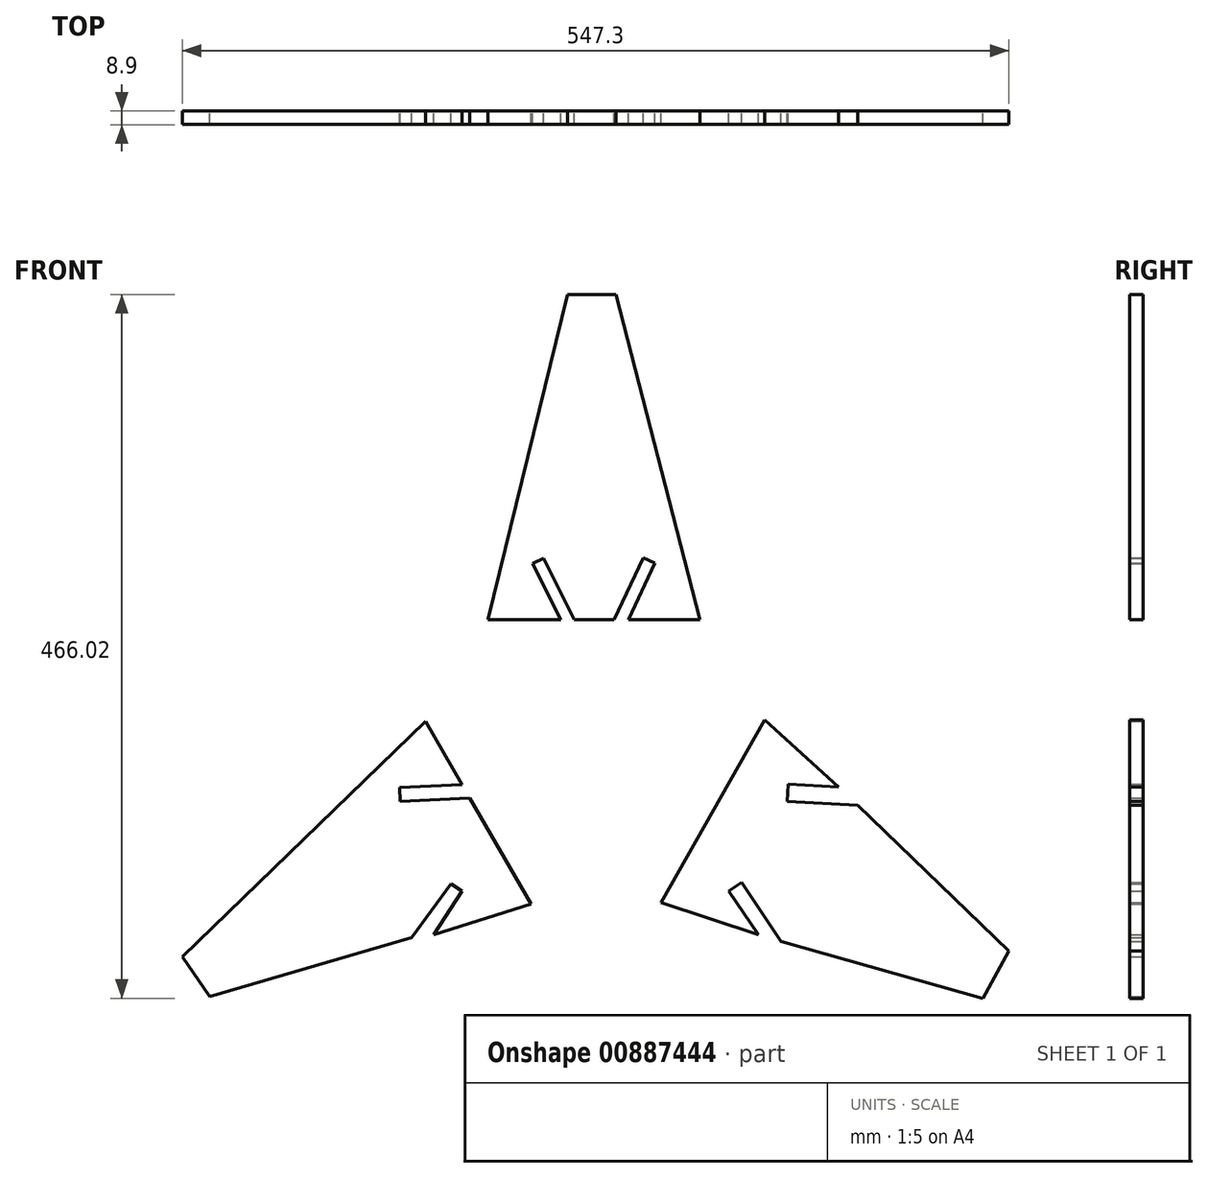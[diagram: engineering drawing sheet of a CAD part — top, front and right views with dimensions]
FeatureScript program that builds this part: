
annotation { "Feature Type Name" : "Feature", "Feature Type Description" : "" }
export const myFeature = defineFeature(function(context is Context, id is Id, definition is map)
    precondition{}
    {
        {
            var Q0;
            Q0=qCreatedBy(makeId("Front.planeOp"),FACE);
            var sketch = newSketch(context, id + "F0", { "sketchPlane" : qUnion([Q0])});
            skLineSegment(sketch, "E0", {"start": v(198.95, 271.23) * mm, "end": v(223.16, 229.27) * mm});
            skLineSegment(sketch, "E1", {"start": v(268.64, 150.43) * mm, "end": v(204.33, 130.14) * mm});
            skLineSegment(sketch, "E2", {"start": v(204.33, 130.14) * mm, "end": v(223.16, 158.75) * mm});
            skLineSegment(sketch, "E3", {"start": v(223.16, 158.75) * mm, "end": v(215.63, 163.7) * mm});
            skLineSegment(sketch, "E4", {"start": v(215.63, 163.7) * mm, "end": v(189.66, 127.94) * mm});
            skLineSegment(sketch, "E5", {"start": v(189.66, 127.94) * mm, "end": v(55.9, 89.06) * mm});
            skLineSegment(sketch, "E6", {"start": v(55.9, 89.06) * mm, "end": v(37.81, 115.47) * mm});
            skLineSegment(sketch, "E7", {"start": v(37.81, 115.47) * mm, "end": v(198.95, 271.23) * mm});
            skLineSegment(sketch, "E8", {"start": v(223.16, 229.27) * mm, "end": v(181.84, 227.46) * mm});
            skLineSegment(sketch, "E9", {"start": v(181.84, 227.46) * mm, "end": v(182.23, 218.4) * mm});
            skLineSegment(sketch, "E10", {"start": v(182.23, 218.4) * mm, "end": v(228.27, 220.41) * mm});
            skLineSegment(sketch, "E11.trimOffspring", {"start": v(228.27, 220.41) * mm, "end": v(268.64, 150.43) * mm});
            skSolve(sketch);
        }
        {
            var Q0;
            Q0 = qSketchRegion(id + "F0", true);
            extrude(context, id + "F1", {"entities" : qUnion([Q0]), "endBound" : BoundingType.SYMMETRIC, "depth" : 8.9 * mm, "offsetDistance" : 25.4 * mm});
        }
        {
            var Q0;
            Q0=qCreatedBy(makeId("Front.planeOp"),FACE);
            var sketch = newSketch(context, id + "F2", { "sketchPlane" : qUnion([Q0])});
            skLineSegment(sketch, "E12", {"start": v(423.52, 272.2) * mm, "end": v(354.7, 151.15) * mm});
            skLineSegment(sketch, "E13", {"start": v(354.7, 151.15) * mm, "end": v(419.1, 129.91) * mm});
            skLineSegment(sketch, "E14", {"start": v(419.1, 129.91) * mm, "end": v(399.72, 158.77) * mm});
            skLineSegment(sketch, "E15", {"start": v(399.72, 158.77) * mm, "end": v(408.17, 164.45) * mm});
            skLineSegment(sketch, "E16", {"start": v(408.17, 164.45) * mm, "end": v(434.22, 125.68) * mm});
            skLineSegment(sketch, "E17", {"start": v(434.22, 125.68) * mm, "end": v(567.8, 87.9) * mm});
            skLineSegment(sketch, "E18", {"start": v(567.8, 87.9) * mm, "end": v(585.11, 119.3) * mm});
            skLineSegment(sketch, "E19", {"start": v(585.11, 119.3) * mm, "end": v(484.9, 215.8) * mm});
            skLineSegment(sketch, "E20", {"start": v(484.9, 215.8) * mm, "end": v(438.27, 218.34) * mm});
            skLineSegment(sketch, "E21", {"start": v(438.27, 218.34) * mm, "end": v(438.9, 229.7) * mm});
            skLineSegment(sketch, "E22", {"start": v(438.9, 229.7) * mm, "end": v(472.18, 227.9) * mm});
            skLineSegment(sketch, "E23", {"start": v(472.18, 227.9) * mm, "end": v(423.52, 272.2) * mm});
            skSolve(sketch);
        }
        {
            var Q0;
            Q0 = qSketchRegion(id + "F2", true);
            extrude(context, id + "F3", {"entities" : qUnion([Q0]), "endBound" : BoundingType.SYMMETRIC, "depth" : 8.9 * mm, "offsetDistance" : 25.4 * mm});
        }
        {
            var Q0;
            Q0=qCreatedBy(makeId("Front.planeOp"),FACE);
            var sketch = newSketch(context, id + "F4", { "sketchPlane" : qUnion([Q0])});
            skLineSegment(sketch, "E24", {"start": v(240.13, 338.63) * mm, "end": v(292.97, 553.91) * mm});
            skLineSegment(sketch, "E25", {"start": v(292.97, 553.91) * mm, "end": v(325, 553.91) * mm});
            skLineSegment(sketch, "E26", {"start": v(325, 553.91) * mm, "end": v(380.38, 338.55) * mm});
            skLineSegment(sketch, "E27", {"start": v(380.38, 338.55) * mm, "end": v(333.11, 338.55) * mm});
            skLineSegment(sketch, "E28", {"start": v(333.11, 338.55) * mm, "end": v(350.78, 375.95) * mm});
            skLineSegment(sketch, "E29", {"start": v(350.78, 375.95) * mm, "end": v(342.96, 379.64) * mm});
            skLineSegment(sketch, "E30", {"start": v(342.96, 379.64) * mm, "end": v(323.63, 338.72) * mm});
            skLineSegment(sketch, "E31", {"start": v(323.63, 338.72) * mm, "end": v(297.32, 338.72) * mm});
            skLineSegment(sketch, "E32", {"start": v(297.32, 338.72) * mm, "end": v(276.9, 379.39) * mm});
            skLineSegment(sketch, "E33", {"start": v(276.9, 379.39) * mm, "end": v(269.66, 375.75) * mm});
            skLineSegment(sketch, "E34", {"start": v(269.66, 375.75) * mm, "end": v(288.34, 338.53) * mm});
            skLineSegment(sketch, "E35", {"start": v(288.34, 338.53) * mm, "end": v(240.13, 338.63) * mm});
            skSolve(sketch);
        }
        {
            var Q0;
            Q0 = qSketchRegion(id + "F4", true);
            extrude(context, id + "F5", {"entities" : qUnion([Q0]), "endBound" : BoundingType.SYMMETRIC, "depth" : 8.9 * mm, "offsetDistance" : 25.4 * mm});
        }
    });
